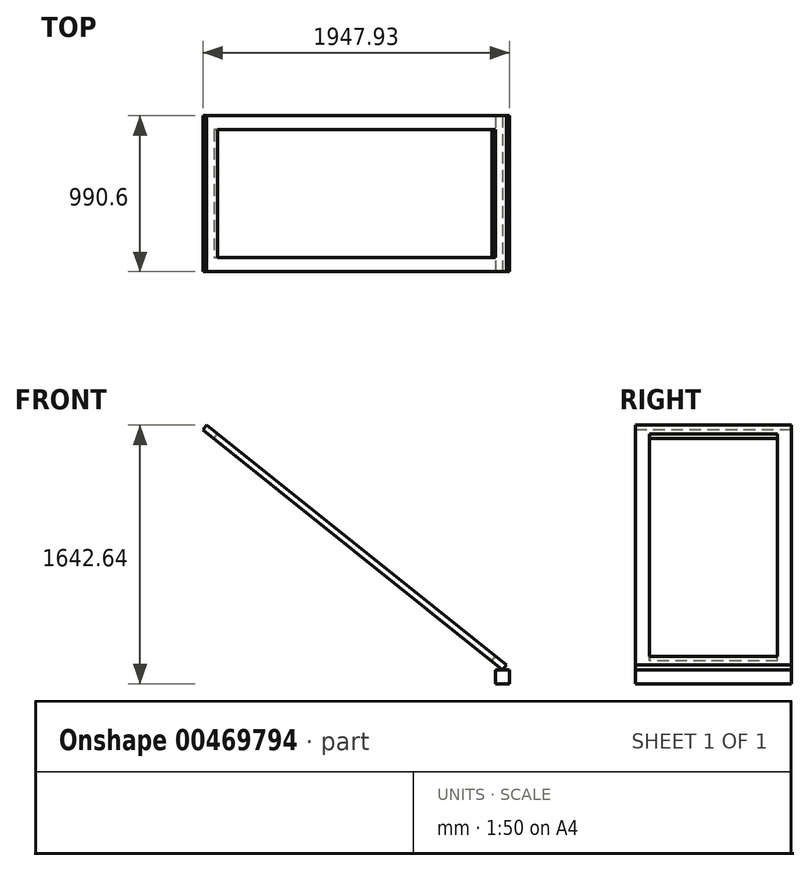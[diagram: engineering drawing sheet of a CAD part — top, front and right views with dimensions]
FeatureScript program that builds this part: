
annotation { "Feature Type Name" : "Feature", "Feature Type Description" : "" }
export const myFeature = defineFeature(function(context is Context, id is Id, definition is map)
    precondition{}
    {
        {
            var Q0;
            Q0=qCreatedBy(makeId("Front.planeOp"),FACE);
            var sketch = newSketch(context, id + "F0", { "sketchPlane" : qUnion([Q0])});
            skLineSegment(sketch, "E0", {"start": v(1947.93, 0) * mm, "end": v(0, 0) * mm, "construction": true});
            skLineSegment(sketch, "E1", {"start": v(0, 0) * mm, "end": v(0, 1612.9) * mm, "construction": true});
            skLineSegment(sketch, "E2", {"start": v(0, 1612.9) * mm, "end": v(1947.93, 0) * mm, "construction": true});
            skLineSegment(sketch, "E3.bottom", {"start": v(1947.93, 0) * mm, "end": v(1859.03, 0) * mm});
            skLineSegment(sketch, "E3.top", {"start": v(1947.93, 88.9) * mm, "end": v(1859.03, 88.9) * mm});
            skLineSegment(sketch, "E3.left", {"start": v(1947.93, 0) * mm, "end": v(1947.93, 88.9) * mm});
            skLineSegment(sketch, "E3.right", {"start": v(1859.03, 0) * mm, "end": v(1859.03, 88.9) * mm});
            skLineSegment(sketch, "E4", {"start": v(0, 1612.9) * mm, "end": v(1903.48, 88.9) * mm, "construction": true});
            skSolve(sketch);
        }
        {
            var Q0;
            Q0=qSketchRegion(id+"F0",true);
            extrude(context, id + "F1", {"entities" : qUnion([Q0]), "oppositeDirection" : true, "depth" : 990.6 * mm});
        }
        {
            var Q0;
            Q0=qCreatedBy(makeId("Front.planeOp"),FACE);
            var sketch = newSketch(context, id + "F2", { "sketchPlane" : qUnion([Q0])});
            skLineSegment(sketch, "E5.bottom", {"start": v(23.81, 1642.64) * mm, "end": v(1927.29, 118.64) * mm});
            skLineSegment(sketch, "E5.top", {"start": v(0, 1612.9) * mm, "end": v(1903.48, 88.9) * mm});
            skLineSegment(sketch, "E5.left", {"start": v(23.81, 1642.64) * mm, "end": v(0, 1612.9) * mm});
            skLineSegment(sketch, "E5.right", {"start": v(1927.29, 118.64) * mm, "end": v(1903.48, 88.9) * mm});
            skSolve(sketch);
        }
        {
            var Q0;
            Q0=qSketchRegion(id+"F2",true);
            extrude(context, id + "F3", {"entities" : qUnion([Q0]), "oppositeDirection" : true, "depth" : 88.9 * mm});
        }
        {
            var Q0;
            Q0=makeQuery(id+"F3.opExtrude","CAP_FACE",FACE,{"disambiguationData":[OSD([sQuery(id+"F2.wireOp",EDGE,"E5.bottom"),sQuery(id+"F2.wireOp",EDGE,"E5.top"),sQuery(id+"F2.wireOp",EDGE,"E5.left"),sQuery(id+"F2.wireOp",EDGE,"E5.right")])],"isStart":false});
            var sketch = newSketch(context, id + "F4", { "sketchPlane" : qUnion([Q0])});
            skLineSegment(sketch, "E6.bottom", {"start": v(0, 1612.9) * mm, "end": v(-69.4, 1557.34) * mm});
            skLineSegment(sketch, "E6.top", {"start": v(-23.81, 1642.64) * mm, "end": v(-93.21, 1587.08) * mm});
            skLineSegment(sketch, "E6.left", {"start": v(0, 1612.9) * mm, "end": v(-23.81, 1642.64) * mm});
            skLineSegment(sketch, "E6.right", {"start": v(-69.4, 1557.34) * mm, "end": v(-93.21, 1587.08) * mm});
            skLineSegment(sketch, "E7.bottom", {"start": v(-1903.48, 88.9) * mm, "end": v(-1834.08, 144.46) * mm});
            skLineSegment(sketch, "E7.top", {"start": v(-1927.29, 118.64) * mm, "end": v(-1857.9, 174.2) * mm});
            skLineSegment(sketch, "E7.left", {"start": v(-1903.48, 88.9) * mm, "end": v(-1927.29, 118.64) * mm});
            skLineSegment(sketch, "E7.right", {"start": v(-1834.08, 144.46) * mm, "end": v(-1857.9, 174.2) * mm});
            skSolve(sketch);
        }
        {
            var Q0;
            Q0=qSketchRegion(id+"F4",true);
            extrude(context, id + "F5", {"entities" : qUnion([Q0]), "operationType" : NewBodyOperationType.ADD, "depth" : 812.8 * mm});
        }
        {
            var Q0;
            Q0=makeQuery(id+"F5.opExtrude","CAP_FACE",FACE,{"disambiguationData":[OSD([sQuery(id+"F4.wireOp",EDGE,"E6.bottom"),sQuery(id+"F4.wireOp",EDGE,"E6.top"),sQuery(id+"F4.wireOp",EDGE,"E6.left"),sQuery(id+"F4.wireOp",EDGE,"E6.right")])],"isStart":false});
            var sketch = newSketch(context, id + "F6", { "sketchPlane" : qUnion([Q0])});
            skLineSegment(sketch, "E8.bottom", {"start": v(-1903.48, 88.9) * mm, "end": v(0, 1612.9) * mm});
            skLineSegment(sketch, "E8.top", {"start": v(-1927.29, 118.64) * mm, "end": v(-23.81, 1642.64) * mm});
            skLineSegment(sketch, "E8.left", {"start": v(-1903.48, 88.9) * mm, "end": v(-1927.29, 118.64) * mm});
            skLineSegment(sketch, "E8.right", {"start": v(0, 1612.9) * mm, "end": v(-23.81, 1642.64) * mm});
            skSolve(sketch);
        }
        {
            var Q0;
            Q0=qSketchRegion(id+"F6",true);
            extrude(context, id + "F7", {"entities" : qUnion([Q0]), "operationType" : NewBodyOperationType.ADD, "depth" : 88.9 * mm});
        }
    });
